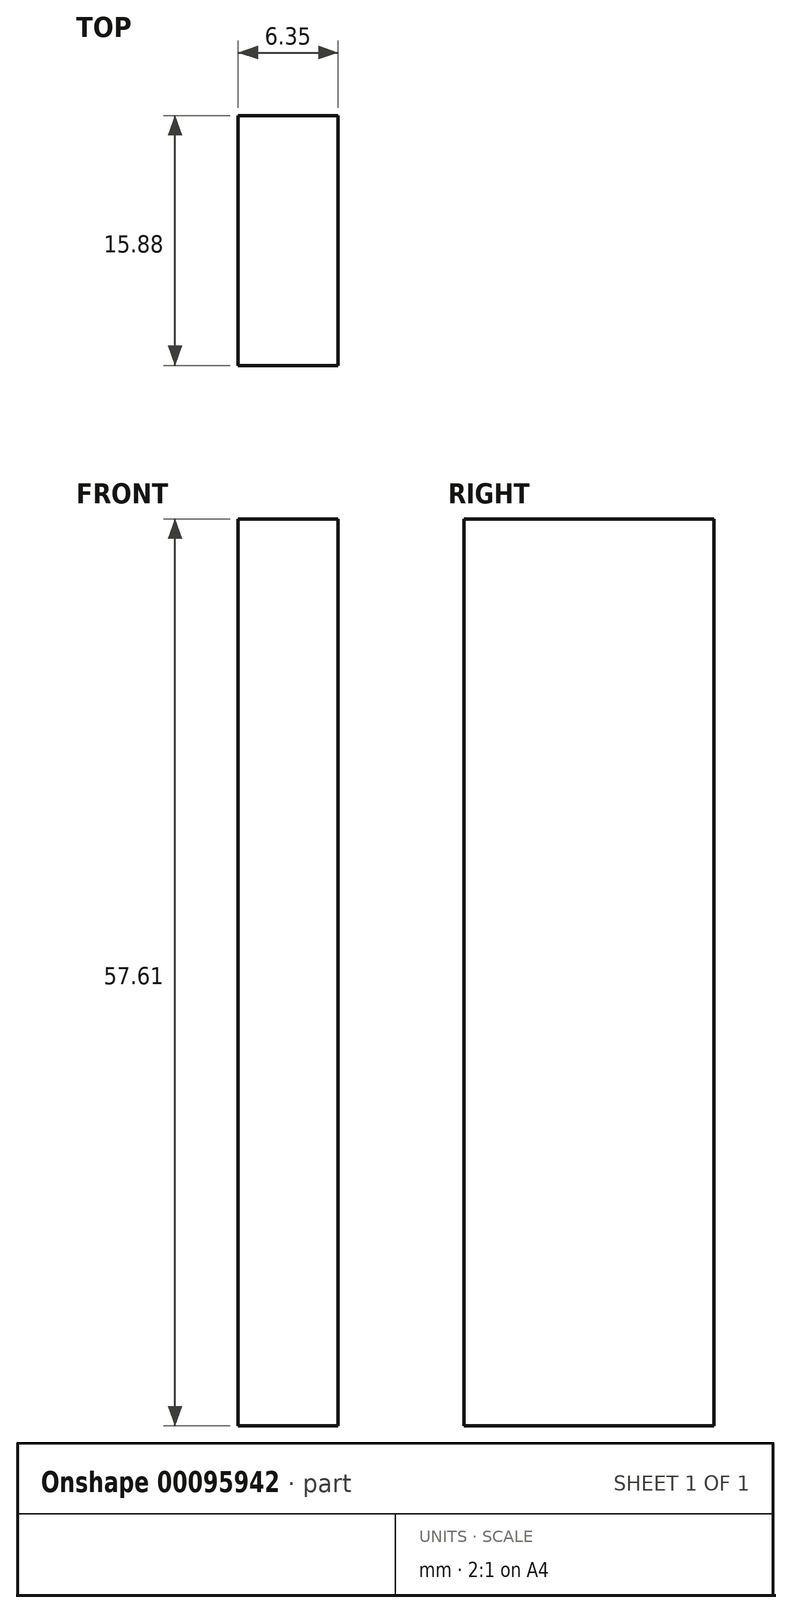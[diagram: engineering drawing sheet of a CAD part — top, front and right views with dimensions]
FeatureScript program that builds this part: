
annotation { "Feature Type Name" : "Feature", "Feature Type Description" : "" }
export const myFeature = defineFeature(function(context is Context, id is Id, definition is map)
    precondition{}
    {
        {
            var Q0;
            Q0=qCreatedBy(makeId("Front.planeOp"),FACE);
            var sketch = newSketch(context, id + "F0", { "sketchPlane" : qUnion([Q0])});
            skLineSegment(sketch, "E0", {"start": v(-50.09, 24.93) * mm, "end": v(-50.09, -32.68) * mm});
            skLineSegment(sketch, "E1", {"start": v(-50.09, 24.93) * mm, "end": v(-43.74, 24.93) * mm});
            skLineSegment(sketch, "E2", {"start": v(-43.74, 24.93) * mm, "end": v(-43.74, -32.68) * mm});
            skLineSegment(sketch, "E3", {"start": v(-43.74, -32.68) * mm, "end": v(-50.09, -32.68) * mm});
            skSolve(sketch);
        }
        {
            var Q0;
            Q0=makeQuery(id+"F0.imprint","IMPRINT",FACE,{"disambiguationData":[TD([[makeQuery(id+"F0.imprint","IMPRINT",EDGE,{"derivedFrom":sQuery(id+"F0.wireOp",EDGE,"E0")}),1.0]])]});
            extrude(context, id + "F1", {"entities" : qUnion([Q0]), "endBound" : BoundingType.SYMMETRIC, "depth" : 15.88 * mm});
        }
    });
